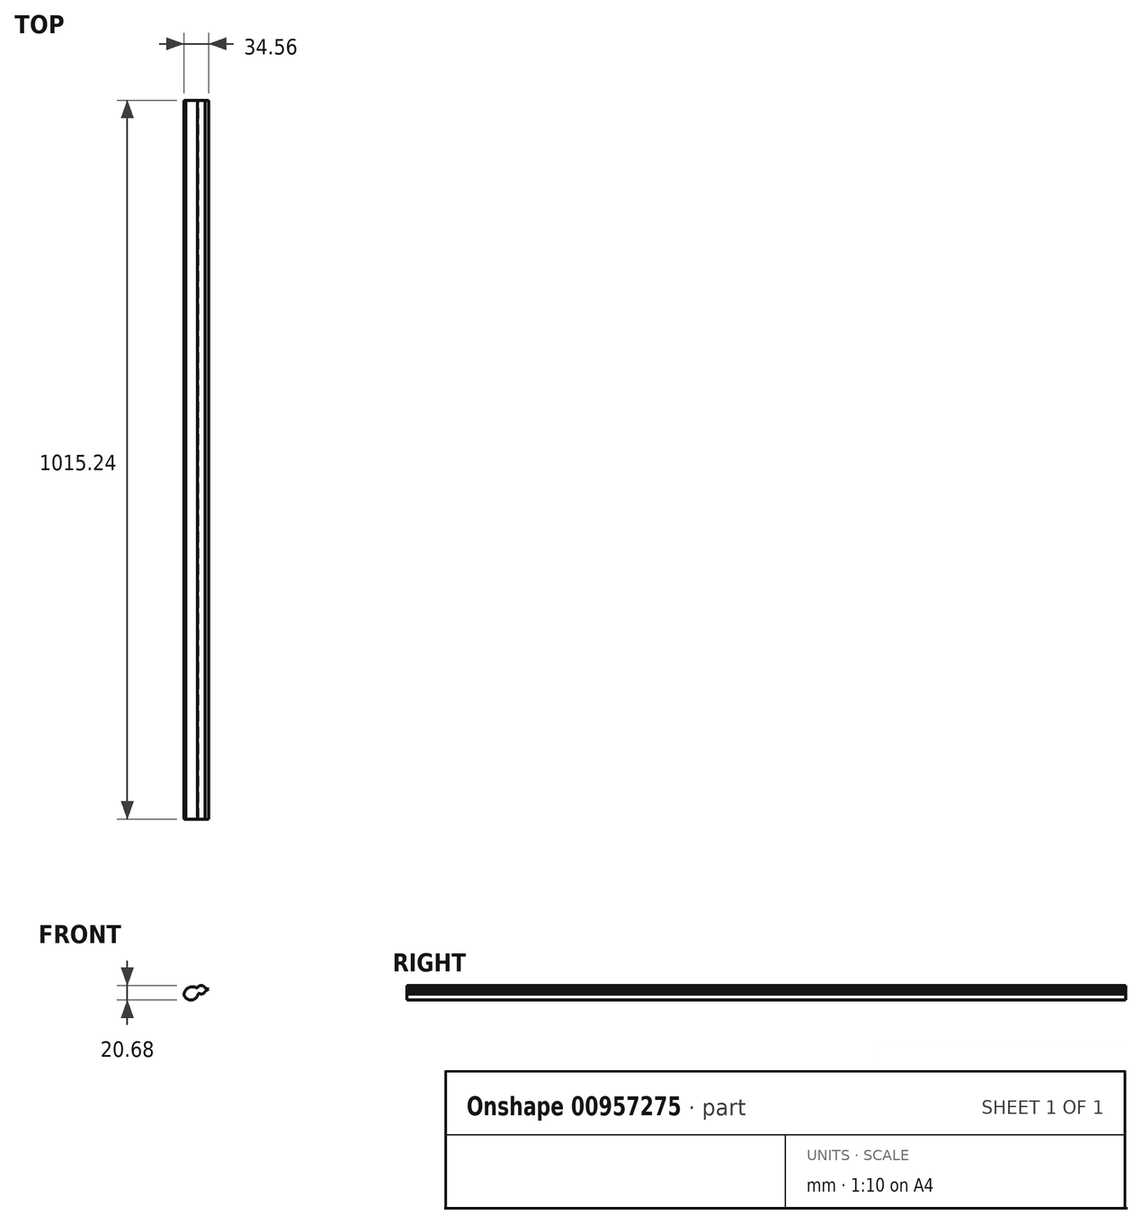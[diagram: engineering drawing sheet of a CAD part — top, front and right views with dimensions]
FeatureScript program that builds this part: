
annotation { "Feature Type Name" : "Feature", "Feature Type Description" : "" }
export const myFeature = defineFeature(function(context is Context, id is Id, definition is map)
    precondition{}
    {
        {
            var Q0;
            Q0=qCreatedBy(makeId("Front.planeOp"),FACE);
            var sketch = newSketch(context, id + "F0", { "sketchPlane" : qUnion([Q0])});
            skCircle(sketch, "E0", {"center": v(15.88, 15.62) * mm, "radius": 6.02 * mm});
            skLineSegment(sketch, "E1", {"start": v(21.53, 17.72) * mm, "end": v(26.12, 16.41) * mm});
            skLineSegment(sketch, "E2", {"start": v(26.12, 16.41) * mm, "end": v(21.73, 14.18) * mm});
            skArc(sketch, "E3", {"start": v(10.27, 17.8) * mm, "mid": v(1.7, 19.7) * mm, "end": v(-5.91, 15.35) * mm});
            skArc(sketch, "E4", {"start": v(-5.91, 15.35) * mm, "mid": v(-7.55, 12.45) * mm, "end": v(-8.44, 9.24) * mm});
            skArc(sketch, "E5", {"start": v(-8.44, 9.24) * mm, "mid": v(1.33, 0.96) * mm, "end": v(11.1, 9.24) * mm});
            skArc(sketch, "E6", {"start": v(11.1, 9.24) * mm, "mid": v(12.14, 9.8) * mm, "end": v(12.03, 10.98) * mm});
            skLineSegment(sketch, "E7", {"start": v(-5.62, 3.81) * mm, "end": v(-6.84, -5.91) * mm});
            skLineSegment(sketch, "E8", {"start": v(-6.84, -5.91) * mm, "end": v(-3.12, -9.5) * mm});
            skLineSegment(sketch, "E9", {"start": v(-3.12, -9.5) * mm, "end": v(-6.84, -5.91) * mm});
            skLineSegment(sketch, "E10", {"start": v(-6.84, -10.57) * mm, "end": v(-6.84, -5.91) * mm});
            skLineSegment(sketch, "E11", {"start": v(-6.84, -5.91) * mm, "end": v(-11.22, -10.45) * mm});
            skLineSegment(sketch, "E12", {"start": v(5.21, 1.76) * mm, "end": v(5.21, -6.45) * mm});
            skLineSegment(sketch, "E13", {"start": v(5.21, -6.45) * mm, "end": v(2.06, -9.77) * mm});
            skLineSegment(sketch, "E14", {"start": v(2.06, -9.77) * mm, "end": v(5.21, -6.45) * mm});
            skLineSegment(sketch, "E15", {"start": v(5.21, -6.45) * mm, "end": v(5.21, -10.3) * mm});
            skLineSegment(sketch, "E16", {"start": v(5.21, -10.3) * mm, "end": v(5.21, -6.45) * mm});
            skLineSegment(sketch, "E17", {"start": v(5.21, -6.45) * mm, "end": v(9.28, -10.3) * mm});
            skSolve(sketch);
        }
        {
            var Q0;
            {var subQ0=sQuery(id+"F0.wireOp",EDGE,"E0");var subQ1=makeQuery(id+"F0.imprint","INTERSECT",VERTEX,{"derivedFrom":[subQ0,sQuery(id+"F0.wireOp",EDGE,"E1")]});Q0=makeQuery(id+"F0.imprint","IMPRINT",FACE,{"disambiguationData":[TD([[makeQuery(id+"F0.imprint","IMPRINT",EDGE,{"disambiguationData":[TD([[subQ1,-1.0]])],"derivedFrom":subQ0}),1.0]])]});}
            var Q1;
            {var subQ0=sQuery(id+"F0.wireOp",EDGE,"E1");Q1=makeQuery(id+"F0.imprint","IMPRINT",FACE,{"disambiguationData":[TD([[makeQuery(id+"F0.imprint","IMPRINT",EDGE,{"derivedFrom":subQ0}),-1.0]])]});}
            var Q2;
            {var subQ3=sQuery(id+"F0.wireOp",EDGE,"E3");Q2=makeQuery(id+"F0.imprint","IMPRINT",FACE,{"disambiguationData":[TD([[makeQuery(id+"F0.imprint","IMPRINT",EDGE,{"derivedFrom":subQ3}),1.0]])]});}
            extrude(context, id + "F1", {"entities" : qUnion([Q0, Q1, Q2]), "depth" : 1015.24 * mm, "offsetDistance" : 25.4 * mm});
        }
    });
